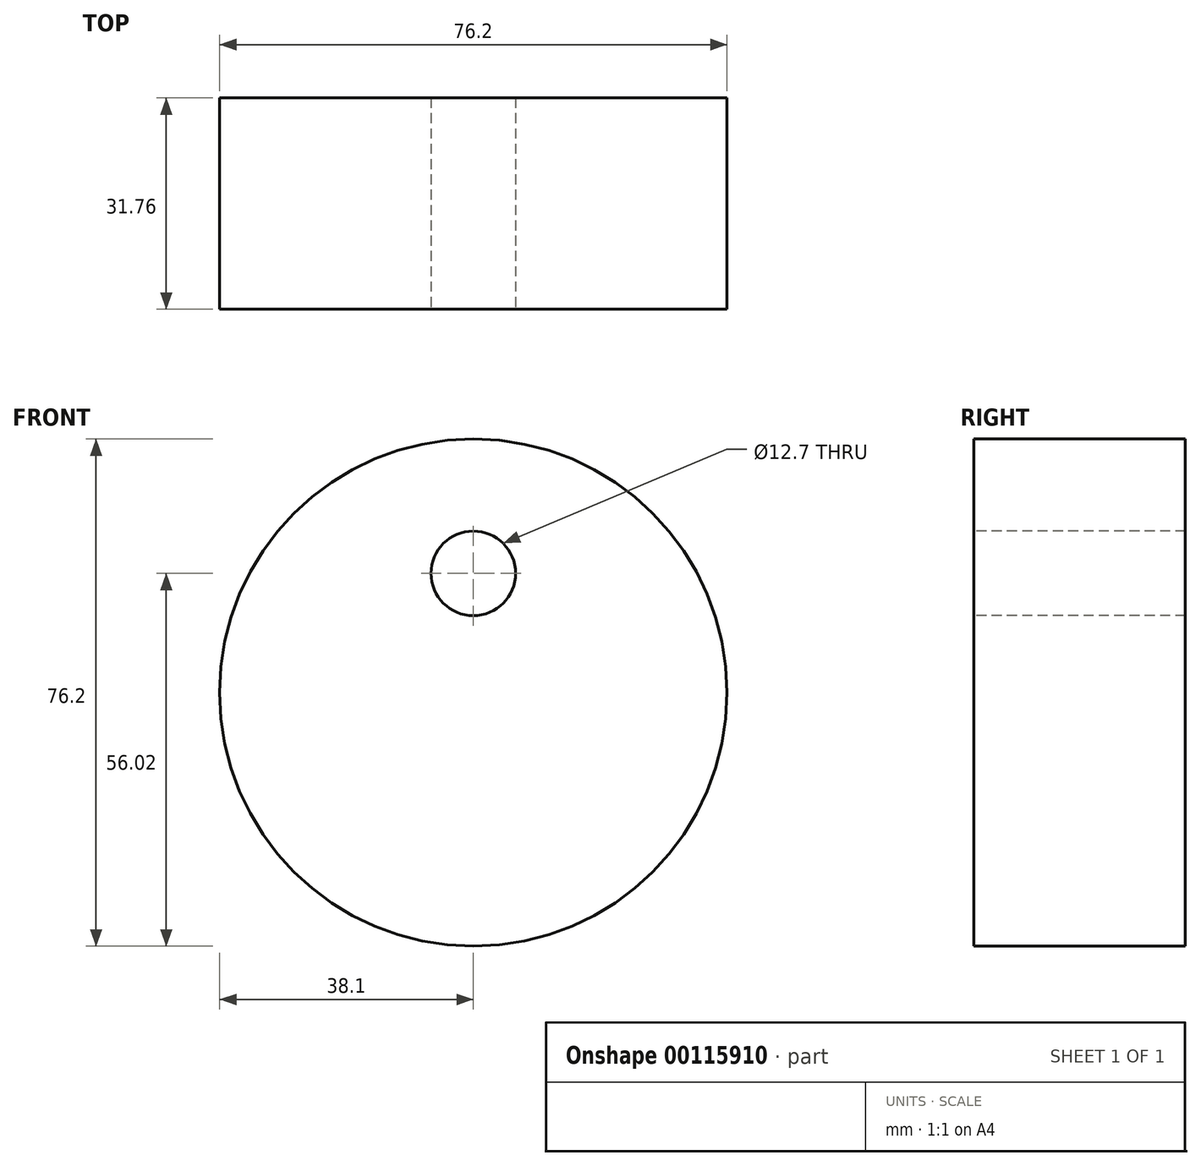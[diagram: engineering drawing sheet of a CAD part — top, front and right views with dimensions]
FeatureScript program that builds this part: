
annotation { "Feature Type Name" : "Feature", "Feature Type Description" : "" }
export const myFeature = defineFeature(function(context is Context, id is Id, definition is map)
    precondition{}
    {
        {
            var Q0;
            Q0=qCreatedBy(makeId("Front.planeOp"),FACE);
            var sketch = newSketch(context, id + "F0", { "sketchPlane" : qUnion([Q0])});
            skCircle(sketch, "E0", {"center": v(0, 0) * mm, "radius": 38.1 * mm});
            skSolve(sketch);
        }
        {
            var Q0;
            Q0 = qSketchRegion(id + "F0", true);
            extrude(context, id + "F1", {"entities" : qUnion([Q0]), "endBound" : BoundingType.SYMMETRIC, "depth" : 31.75 * mm});
        }
        {
            var Q0;
            Q0=qCreatedBy(makeId("Front.planeOp"),FACE);
            var sketch = newSketch(context, id + "F2", { "sketchPlane" : qUnion([Q0])});
            skCircle(sketch, "E1", {"center": v(0, 17.92) * mm, "radius": 6.35 * mm});
            skSolve(sketch);
        }
        {
            var Q0;
            Q0 = qSketchRegion(id + "F2", true);
            extrude(context, id + "F3", {"entities" : qUnion([Q0]), "operationType" : NewBodyOperationType.REMOVE, "endBound" : BoundingType.SYMMETRIC, "oppositeDirection" : true, "depth" : 31.75 * mm});
        }
    });
